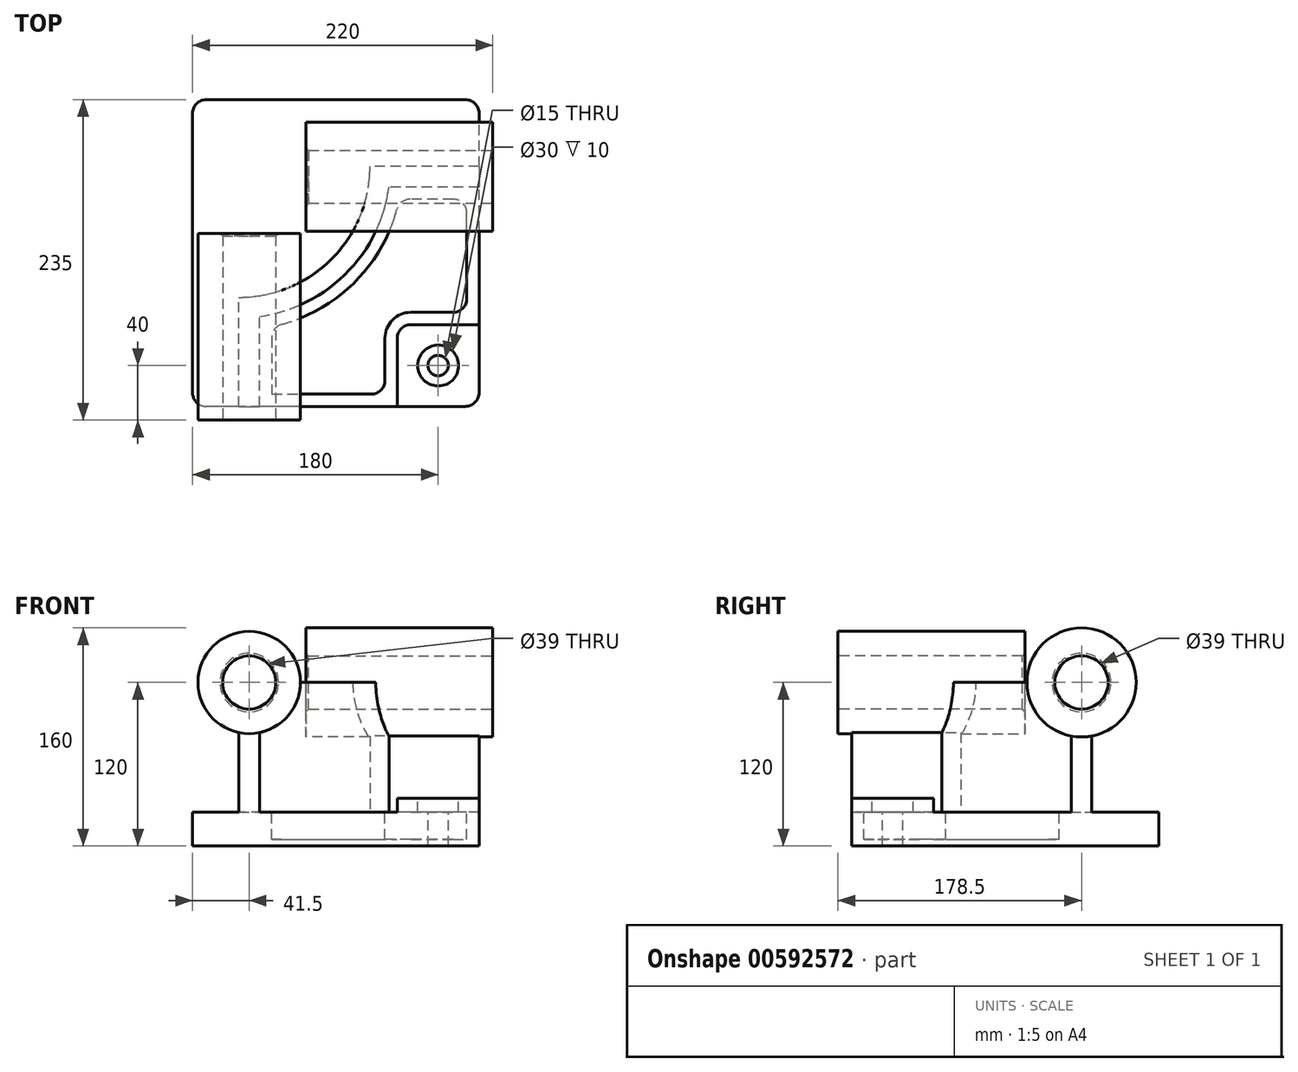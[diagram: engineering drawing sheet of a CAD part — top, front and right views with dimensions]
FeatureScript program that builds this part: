
annotation { "Feature Type Name" : "Feature", "Feature Type Description" : "" }
export const myFeature = defineFeature(function(context is Context, id is Id, definition is map)
    precondition{}
    {
        {
            var Q0;
            Q0=qCreatedBy(makeId("Top.planeOp"),FACE);
            var sketch = newSketch(context, id + "F0", { "sketchPlane" : qUnion([Q0])});
            skLineSegment(sketch, "E0.bottom", {"start": v(105, -112.5) * mm, "end": v(-105, -112.5) * mm});
            skLineSegment(sketch, "E0.top", {"start": v(105, 112.5) * mm, "end": v(-105, 112.5) * mm});
            skLineSegment(sketch, "E0.left", {"start": v(105, -112.5) * mm, "end": v(105, 112.5) * mm});
            skLineSegment(sketch, "E0.right", {"start": v(-105, -112.5) * mm, "end": v(-105, 112.5) * mm});
            skPoint(sketch, "E0.middle", {"position": v(0, 0) * mm});
            skSolve(sketch);
        }
        {
            var Q0;
            Q0=makeQuery(id+"F0.imprint","IMPRINT",FACE,{"disambiguationData":[TD([[makeQuery(id+"F0.imprint","IMPRINT",EDGE,{"derivedFrom":sQuery(id+"F0.wireOp",EDGE,"E0.bottom")}),-1.0]])]});
            extrude(context, id + "F1", {"entities" : qUnion([Q0]), "depth" : 25 * mm, "offsetDistance" : 25 * mm});
        }
        {
            var Q0;
            Q0=makeQuery(id+"F1.opExtrude","CAP_FACE",FACE,{"disambiguationData":[OSD([sQuery(id+"F0.wireOp",EDGE,"E0.bottom"),sQuery(id+"F0.wireOp",EDGE,"E0.top"),sQuery(id+"F0.wireOp",EDGE,"E0.left"),sQuery(id+"F0.wireOp",EDGE,"E0.right")])],"isStart":false});
            var sketch = newSketch(context, id + "F2", { "sketchPlane" : qUnion([Q0])});
            skLineSegment(sketch, "E1", {"start": v(-71, -112.5) * mm, "end": v(-71, -32.5) * mm});
            skLineSegment(sketch, "E2", {"start": v(105, 63.5) * mm, "end": v(25, 63.5) * mm});
            skArc(sketch, "E3", {"start": v(-71, -32.5) * mm, "mid": v(-3.12, -4.38) * mm, "end": v(25, 63.5) * mm});
            skLineSegment(sketch, "E4", {"start": v(-71, 63.5) * mm, "end": v(25, 63.5) * mm, "construction": true});
            skLineSegment(sketch, "E5", {"start": v(-71, 63.5) * mm, "end": v(-71, -32.5) * mm, "construction": true});
            skLineSegment(sketch, "E6.0", {"start": v(-56, -112.5) * mm, "end": v(-56, -46.48) * mm});
            skArc(sketch, "E6.1", {"start": v(-56, -46.48) * mm, "mid": v(7.49, -14.99) * mm, "end": v(38.98, 48.5) * mm});
            skLineSegment(sketch, "E6.2", {"start": v(105, 48.5) * mm, "end": v(38.98, 48.5) * mm});
            skLineSegment(sketch, "E7.0", {"start": v(105, -112.5) * mm, "end": v(105, 112.5) * mm});
            skLineSegment(sketch, "E8.0", {"start": v(105, -112.5) * mm, "end": v(-105, -112.5) * mm});
            skSolve(sketch);
        }
        {
            var Q0;
            {var subQ2=sQuery(id+"F2.wireOp",EDGE,"E1");Q0=makeQuery(id+"F2.imprint","IMPRINT",FACE,{"disambiguationData":[TD([[makeQuery(id+"F2.imprint","IMPRINT",EDGE,{"derivedFrom":subQ2}),-1.0]])]});}
            extrude(context, id + "F3", {"entities" : qUnion([Q0]), "operationType" : NewBodyOperationType.ADD, "depth" : 95 * mm, "offsetDistance" : 25 * mm});
        }
        {
            var Q0;
            Q0=makeQuery(id+"F3.boolean.opBoolean","MERGE",FACE,{"derivedFrom":[makeQuery(id+"F1.opExtrude","SWEPT_FACE",FACE,{"disambiguationData":[OSD([sQuery(id+"F0.wireOp",EDGE,"E0.bottom")])]}),makeQuery(id+"F3.opExtrude","SWEPT_FACE",FACE,{"disambiguationData":[OSD([sQuery(id+"F2.wireOp",EDGE,"E8.0")])]})]});
            var sketch = newSketch(context, id + "F4", { "sketchPlane" : qUnion([Q0])});
            skCircle(sketch, "E9", {"center": v(-63.5, 120) * mm, "radius": 37.5 * mm});
            skSolve(sketch);
        }
        {
            var Q0;
            Q0 = qSketchRegion(id + "F4", true);
            extrude(context, id + "F5", {"entities" : qUnion([Q0]), "operationType" : NewBodyOperationType.ADD, "depth" : 10 * mm, "offsetDistance" : 25 * mm, "hasSecondDirection" : true, "secondDirectionOppositeDirection" : true, "secondDirectionDepth" : 127 * mm});
        }
        {
            var Q0;
            Q0=makeQuery(id+"F3.boolean.opBoolean","MERGE",FACE,{"derivedFrom":[makeQuery(id+"F1.opExtrude","SWEPT_FACE",FACE,{"disambiguationData":[OSD([sQuery(id+"F0.wireOp",EDGE,"E0.left")])]}),makeQuery(id+"F3.opExtrude","SWEPT_FACE",FACE,{"disambiguationData":[OSD([sQuery(id+"F2.wireOp",EDGE,"E7.0")])]})]});
            var sketch = newSketch(context, id + "F6", { "sketchPlane" : qUnion([Q0])});
            skCircle(sketch, "E10", {"center": v(56, 120) * mm, "radius": 40 * mm});
            skSolve(sketch);
        }
        {
            var Q0;
            Q0 = qSketchRegion(id + "F6", true);
            extrude(context, id + "F7", {"entities" : qUnion([Q0]), "operationType" : NewBodyOperationType.ADD, "depth" : 10 * mm, "offsetDistance" : 25 * mm, "hasSecondDirection" : true, "secondDirectionOppositeDirection" : true, "secondDirectionDepth" : 127 * mm});
        }
        {
            var Q0;
            {var subQ0=sQuery(id+"F0.wireOp",EDGE,"E0.left");var subQ1=sQuery(id+"F0.wireOp",EDGE,"E0.bottom");Q0=makeQuery(id+"F3.boolean.opBoolean","SPLIT",FACE,{"disambiguationData":[TD([makeQuery(id+"F3.opExtrude","SWEPT_FACE",FACE,{"disambiguationData":[OSD([sQuery(id+"F2.wireOp",EDGE,"E6.0")])]})])],"derivedFrom":makeQuery(id+"F1.opExtrude","CAP_FACE",FACE,{"disambiguationData":[OSD([subQ1,sQuery(id+"F0.wireOp",EDGE,"E0.top"),subQ0,sQuery(id+"F0.wireOp",EDGE,"E0.right")])],"isStart":false})});}
            var sketch = newSketch(context, id + "F8", { "sketchPlane" : qUnion([Q0])});
            skLineSegment(sketch, "E11.bottom", {"start": v(105, -112.5) * mm, "end": v(45, -112.5) * mm});
            skLineSegment(sketch, "E11.top", {"start": v(105, -52.5) * mm, "end": v(45, -52.5) * mm});
            skLineSegment(sketch, "E11.left", {"start": v(105, -112.5) * mm, "end": v(105, -52.5) * mm});
            skLineSegment(sketch, "E11.right", {"start": v(45, -112.5) * mm, "end": v(45, -52.5) * mm});
            skSolve(sketch);
        }
        {
            var Q0;
            Q0 = qSketchRegion(id + "F8", true);
            extrude(context, id + "F9", {"entities" : qUnion([Q0]), "operationType" : NewBodyOperationType.ADD, "depth" : 10 * mm, "offsetDistance" : 25 * mm});
        }
        {
            var Q0;
            Q0=makeQuery(id+"F9.opExtrude","SWEPT_EDGE",EDGE,{"disambiguationData":[OSD([sQuery(id+"F8.wireOp",EDGE,"E11.top"),sQuery(id+"F8.wireOp",EDGE,"E11.right")])]});
            fillet(context, id + "F10", {"entities" : qUnion([Q0]), "radius" : 10 * mm, "tangentPropagation" : true, "allowEdgeOverflow" : false});
        }
        {
            var Q0;
            {var subQ0=sQuery(id+"F0.wireOp",EDGE,"E0.left");var subQ1=sQuery(id+"F0.wireOp",EDGE,"E0.bottom");Q0=makeQuery(id+"F3.boolean.opBoolean","SPLIT",FACE,{"disambiguationData":[TD([makeQuery(id+"F3.opExtrude","SWEPT_FACE",FACE,{"disambiguationData":[OSD([sQuery(id+"F2.wireOp",EDGE,"E6.0")])]})])],"derivedFrom":makeQuery(id+"F1.opExtrude","CAP_FACE",FACE,{"disambiguationData":[OSD([subQ1,sQuery(id+"F0.wireOp",EDGE,"E0.top"),subQ0,sQuery(id+"F0.wireOp",EDGE,"E0.right")])],"isStart":false})});}
            var sketch = newSketch(context, id + "F11", { "sketchPlane" : qUnion([Q0])});
            skLineSegment(sketch, "E12.0", {"start": v(-47, -54.08) * mm, "end": v(-47, -103.5) * mm});
            skArc(sketch, "E12.1", {"start": v(46.58, 39.5) * mm, "mid": v(13.85, -21.35) * mm, "end": v(-47, -54.08) * mm});
            skLineSegment(sketch, "E12.2", {"start": v(-47, -103.5) * mm, "end": v(36, -103.5) * mm});
            skLineSegment(sketch, "E12.3", {"start": v(96, 39.5) * mm, "end": v(46.58, 39.5) * mm});
            skLineSegment(sketch, "E12.4", {"start": v(36, -103.5) * mm, "end": v(36, -62.5) * mm});
            skArc(sketch, "E12.5", {"start": v(36, -62.5) * mm, "mid": v(41.56, -49.06) * mm, "end": v(55, -43.5) * mm});
            skLineSegment(sketch, "E12.6", {"start": v(55, -43.5) * mm, "end": v(96, -43.5) * mm});
            skLineSegment(sketch, "E12.7", {"start": v(96, -43.5) * mm, "end": v(96, 39.5) * mm});
            skSolve(sketch);
        }
        {
            var Q0;
            Q0=makeQuery(id+"F11.imprint","IMPRINT",FACE,{"disambiguationData":[TD([[makeQuery(id+"F11.imprint","IMPRINT",EDGE,{"derivedFrom":sQuery(id+"F11.wireOp",EDGE,"E12.0")}),1.0]])]});
            extrude(context, id + "F12", {"entities" : qUnion([Q0]), "operationType" : NewBodyOperationType.REMOVE, "oppositeDirection" : true, "depth" : 20 * mm, "offsetDistance" : 25 * mm});
        }
        {
            var Q0;
            Q0=makeQuery(id+"F9.opExtrude","CAP_FACE",FACE,{"disambiguationData":[OSD([sQuery(id+"F8.wireOp",EDGE,"E11.bottom"),sQuery(id+"F8.wireOp",EDGE,"E11.top"),sQuery(id+"F8.wireOp",EDGE,"E11.left"),sQuery(id+"F8.wireOp",EDGE,"E11.right")])],"isStart":false});
            var sketch = newSketch(context, id + "F13", { "sketchPlane" : qUnion([Q0])});
            skCircle(sketch, "E13", {"center": v(75, -82.5) * mm, "radius": 15 * mm});
            skSolve(sketch);
        }
        {
            var Q0;
            Q0=sQuery(id+"F13.wireOp",VERTEX,"E13.center");
            var Q1;
            Q1=makeQuery(id+"F1.opExtrude","SWEPT_BODY",BODY,{"disambiguationData":[OSD([sQuery(id+"F0.wireOp",EDGE,"E0.bottom"),sQuery(id+"F0.wireOp",EDGE,"E0.top"),sQuery(id+"F0.wireOp",EDGE,"E0.left"),sQuery(id+"F0.wireOp",EDGE,"E0.right")])]});
            hole(context, id + "F14", {"style" : HoleStyle.C_BORE, "endStyle" : HoleEndStyle.THROUGH, "holeDiameter" : 15 * mm, "cBoreDiameter" : 30 * mm, "cBoreDepth" : 10 * mm, "majorDiameter" : 5 * mm, "isTappedThrough" : true, "tappedDepth" : 12 * mm, "tapClearance" : 3, "locations" : qUnion([Q0]), "scope" : qUnion([Q1])});
        }
        {
            var Q0;
            Q0=makeQuery(id+"F12.boolean.opBoolean","COPY",EDGE,{"derivedFrom":makeQuery(id+"F12.opExtrude","SWEPT_EDGE",EDGE,{"disambiguationData":[OSD([sQuery(id+"F11.wireOp",EDGE,"E12.0"),sQuery(id+"F11.wireOp",EDGE,"E12.1")])]})});
            var Q1;
            Q1=makeQuery(id+"F12.boolean.opBoolean","COPY",EDGE,{"derivedFrom":makeQuery(id+"F12.opExtrude","SWEPT_EDGE",EDGE,{"disambiguationData":[OSD([sQuery(id+"F11.wireOp",EDGE,"E12.1"),sQuery(id+"F11.wireOp",EDGE,"E12.3")])]})});
            var Q2;
            Q2=makeQuery(id+"F12.boolean.opBoolean","COPY",EDGE,{"derivedFrom":makeQuery(id+"F12.opExtrude","SWEPT_EDGE",EDGE,{"disambiguationData":[OSD([sQuery(id+"F11.wireOp",EDGE,"E12.3"),sQuery(id+"F11.wireOp",EDGE,"E12.7")])]})});
            var Q3;
            Q3=makeQuery(id+"F12.boolean.opBoolean","COPY",EDGE,{"derivedFrom":makeQuery(id+"F12.opExtrude","SWEPT_EDGE",EDGE,{"disambiguationData":[OSD([sQuery(id+"F11.wireOp",EDGE,"E12.2"),sQuery(id+"F11.wireOp",EDGE,"E12.4")])]})});
            var Q4;
            Q4=makeQuery(id+"F12.boolean.opBoolean","COPY",EDGE,{"derivedFrom":makeQuery(id+"F12.opExtrude","SWEPT_EDGE",EDGE,{"disambiguationData":[OSD([sQuery(id+"F11.wireOp",EDGE,"E12.6"),sQuery(id+"F11.wireOp",EDGE,"E12.7")])]})});
            fillet(context, id + "F15", {"entities" : qUnion([Q0, Q1, Q2, Q3, Q4]), "radius" : 10 * mm, "tangentPropagation" : true, "allowEdgeOverflow" : false});
        }
        {
            var Q0;
            Q0=makeQuery(id+"F5.opExtrude","CAP_FACE",FACE,{"disambiguationData":[OSD([sQuery(id+"F4.wireOp",EDGE,"E9")])],"isStart":false});
            var sketch = newSketch(context, id + "F16", { "sketchPlane" : qUnion([Q0])});
            skCircle(sketch, "E14", {"center": v(-63.5, 120) * mm, "radius": 19.5 * mm});
            skSolve(sketch);
        }
        {
            var Q0;
            Q0 = qSketchRegion(id + "F16", true);
            extrude(context, id + "F17", {"entities" : qUnion([Q0]), "operationType" : NewBodyOperationType.REMOVE, "endBound" : BoundingType.THROUGH_ALL, "oppositeDirection" : true, "depth" : 31.5 * mm, "offsetDistance" : 25 * mm});
        }
        {
            var Q0;
            Q0=makeQuery(id+"F7.opExtrude","CAP_FACE",FACE,{"disambiguationData":[OSD([sQuery(id+"F6.wireOp",EDGE,"E10")])],"isStart":false});
            var sketch = newSketch(context, id + "F18", { "sketchPlane" : qUnion([Q0])});
            skCircle(sketch, "E15", {"center": v(56, 120) * mm, "radius": 19.5 * mm});
            skSolve(sketch);
        }
        {
            var Q0;
            Q0 = qSketchRegion(id + "F18", true);
            extrude(context, id + "F19", {"entities" : qUnion([Q0]), "operationType" : NewBodyOperationType.REMOVE, "endBound" : BoundingType.THROUGH_ALL, "oppositeDirection" : true, "depth" : 42 * mm, "offsetDistance" : 25 * mm});
        }
        {
            var Q0;
            Q0=makeQuery(id+"F17.boolean.opBoolean","COPY",EDGE,{"derivedFrom":makeQuery(id+"F17.opExtrude","CAP_EDGE",EDGE,{"disambiguationData":[OSD([sQuery(id+"F16.wireOp",EDGE,"E14")])],"isStart":true})});
            var Q1;
            Q1=makeQuery(id+"F19.boolean.opBoolean","COPY",EDGE,{"derivedFrom":makeQuery(id+"F19.opExtrude","CAP_EDGE",EDGE,{"disambiguationData":[OSD([sQuery(id+"F18.wireOp",EDGE,"E15")])],"isStart":true})});
            var Q2;
            Q2=makeQuery(id+"F17.boolean.opBoolean","INTERSECT",EDGE,{"derivedFrom":[makeQuery(id+"F5.opExtrude","CAP_FACE",FACE,{"disambiguationData":[OSD([sQuery(id+"F4.wireOp",EDGE,"E9")])],"isStart":true}),makeQuery(id+"F17.opExtrude","SWEPT_FACE",FACE,{"disambiguationData":[OSD([sQuery(id+"F16.wireOp",EDGE,"E14")])]})]});
            var Q3;
            Q3=makeQuery(id+"F19.boolean.opBoolean","INTERSECT",EDGE,{"derivedFrom":[makeQuery(id+"F7.opExtrude","CAP_FACE",FACE,{"disambiguationData":[OSD([sQuery(id+"F6.wireOp",EDGE,"E10")])],"isStart":true}),makeQuery(id+"F19.opExtrude","SWEPT_FACE",FACE,{"disambiguationData":[OSD([sQuery(id+"F18.wireOp",EDGE,"E15")])]})]});
            chamfer(context, id + "F20", {"entities" : qUnion([Q0, Q1, Q2, Q3]), "width" : 2 * mm, "tangentPropagation" : true});
        }
        {
            var Q0;
            Q0=makeQuery(id+"F9.boolean.opBoolean","MERGE",EDGE,{"derivedFrom":[makeQuery(id+"F1.opExtrude","SWEPT_EDGE",EDGE,{"disambiguationData":[OSD([sQuery(id+"F0.wireOp",EDGE,"E0.bottom"),sQuery(id+"F0.wireOp",EDGE,"E0.left")])]}),makeQuery(id+"F9.opExtrude","SWEPT_EDGE",EDGE,{"disambiguationData":[OSD([sQuery(id+"F8.wireOp",EDGE,"E11.bottom"),sQuery(id+"F8.wireOp",EDGE,"E11.left")])]})]});
            var Q1;
            Q1=makeQuery(id+"F1.opExtrude","SWEPT_EDGE",EDGE,{"disambiguationData":[OSD([sQuery(id+"F0.wireOp",EDGE,"E0.bottom"),sQuery(id+"F0.wireOp",EDGE,"E0.right")])]});
            var Q2;
            Q2=makeQuery(id+"F1.opExtrude","SWEPT_EDGE",EDGE,{"disambiguationData":[OSD([sQuery(id+"F0.wireOp",EDGE,"E0.top"),sQuery(id+"F0.wireOp",EDGE,"E0.left")])]});
            var Q3;
            Q3=makeQuery(id+"F1.opExtrude","SWEPT_EDGE",EDGE,{"disambiguationData":[OSD([sQuery(id+"F0.wireOp",EDGE,"E0.top"),sQuery(id+"F0.wireOp",EDGE,"E0.right")])]});
            fillet(context, id + "F21", {"entities" : qUnion([Q0, Q1, Q2, Q3]), "radius" : 10 * mm, "tangentPropagation" : true, "allowEdgeOverflow" : false});
        }
    });
